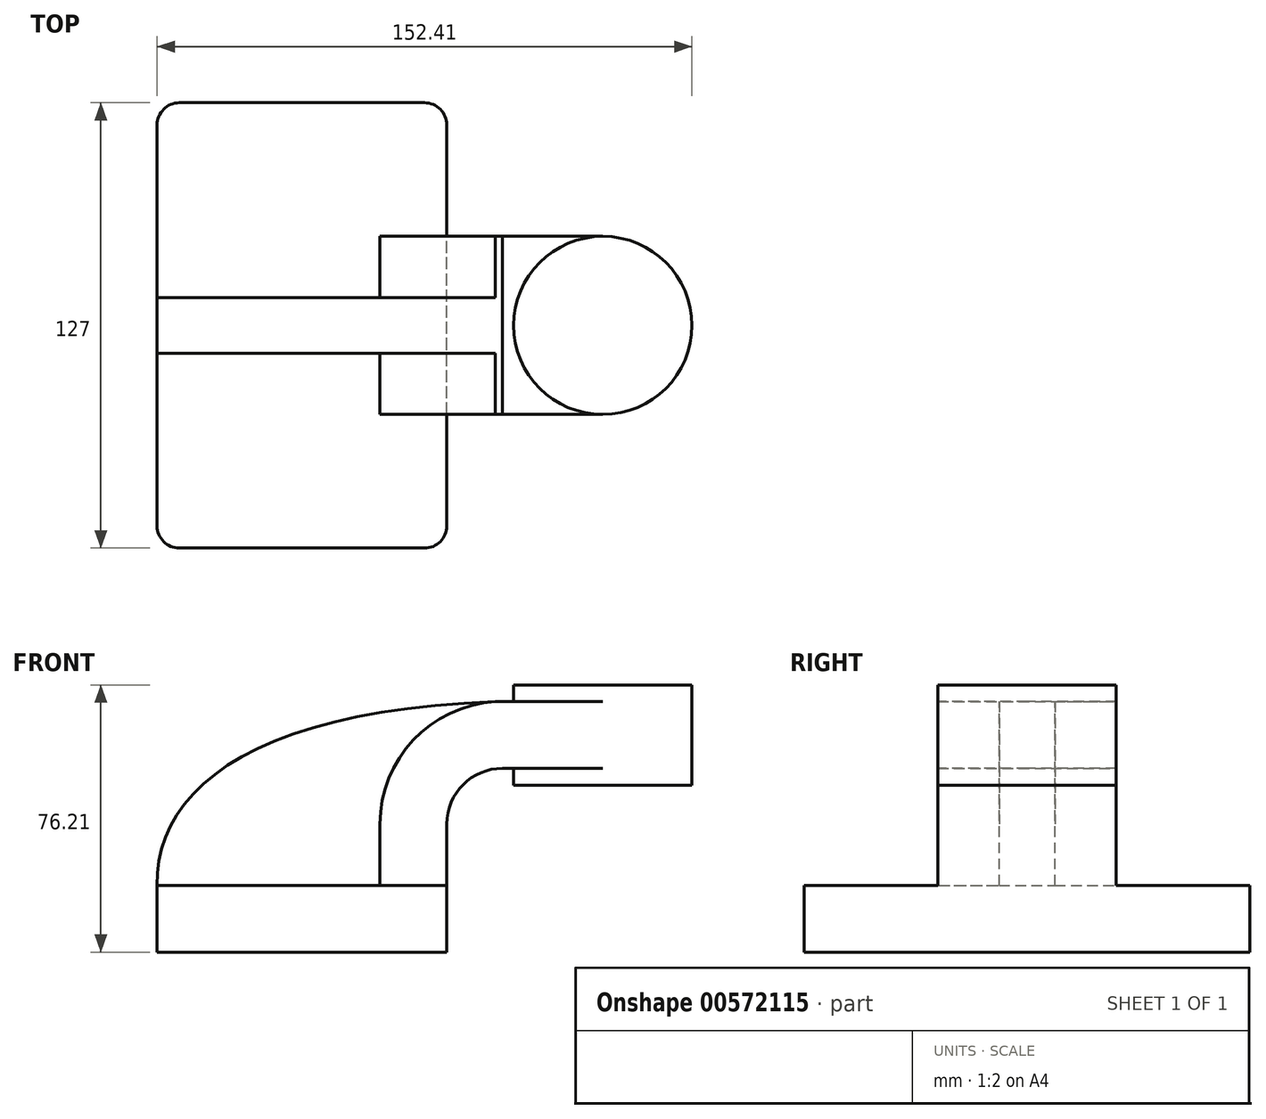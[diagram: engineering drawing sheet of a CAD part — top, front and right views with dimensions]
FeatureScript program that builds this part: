
annotation { "Feature Type Name" : "Feature", "Feature Type Description" : "" }
export const myFeature = defineFeature(function(context is Context, id is Id, definition is map)
    precondition{}
    {
        {
            var Q0;
            Q0=qCreatedBy(makeId("Front.planeOp"),FACE);
            var sketch = newSketch(context, id + "F0", { "sketchPlane" : qUnion([Q0])});
            skLineSegment(sketch, "E0.bottom", {"start": v(41.28, -9.52) * mm, "end": v(-41.28, -9.53) * mm});
            skLineSegment(sketch, "E0.top", {"start": v(41.28, 9.53) * mm, "end": v(-41.28, 9.52) * mm});
            skLineSegment(sketch, "E0.left", {"start": v(41.28, -9.52) * mm, "end": v(41.28, 9.53) * mm});
            skLineSegment(sketch, "E0.right", {"start": v(-41.28, -9.53) * mm, "end": v(-41.28, 9.52) * mm});
            skPoint(sketch, "E0.middle", {"position": v(0, 0) * mm});
            skLineSegment(sketch, "E1.bottom", {"start": v(60.33, 38.1) * mm, "end": v(111.13, 38.1) * mm});
            skLineSegment(sketch, "E1.top", {"start": v(60.33, 66.68) * mm, "end": v(111.13, 66.68) * mm});
            skLineSegment(sketch, "E1.left", {"start": v(60.33, 38.1) * mm, "end": v(60.33, 66.68) * mm});
            skLineSegment(sketch, "E1.right", {"start": v(111.13, 38.1) * mm, "end": v(111.13, 66.68) * mm});
            skPoint(sketch, "E1.middle", {"position": v(85.73, 52.39) * mm});
            skLineSegment(sketch, "E2", {"start": v(41.28, 9.53) * mm, "end": v(41.28, 27) * mm});
            skArc(sketch, "E3", {"start": v(41.28, 27) * mm, "mid": v(45.92, 38.23) * mm, "end": v(57.15, 42.88) * mm});
            skLineSegment(sketch, "E4", {"start": v(57.15, 42.88) * mm, "end": v(85.73, 42.88) * mm});
            skLineSegment(sketch, "E5.0", {"start": v(57.15, 61.93) * mm, "end": v(85.73, 61.93) * mm});
            skArc(sketch, "E5.1", {"start": v(22.23, 27) * mm, "mid": v(32.45, 51.7) * mm, "end": v(57.15, 61.93) * mm});
            skLineSegment(sketch, "E5.2", {"start": v(22.23, 9.53) * mm, "end": v(22.23, 27) * mm});
            skLineSegment(sketch, "E6", {"start": v(85.73, 42.88) * mm, "end": v(85.73, 66.68) * mm});
            skFitSpline(sketch, "E7", {"points": [v(-41.28, 9.52) * mm, v(57.15, 61.93) * mm], "startDerivative": vector(-1.78, 81.87) * mm, "endDerivative": vector(211.67, 5.76) * mm});
            skLineSegment(sketch, "E8", {"start": v(85.73, 42.88) * mm, "end": v(85.72, 38.1) * mm});
            skSolve(sketch);
        }
        {
            var Q0;
            Q0=makeQuery(id+"F0.imprint","IMPRINT",FACE,{"disambiguationData":[TD([[makeQuery(id+"F0.imprint","IMPRINT",EDGE,{"derivedFrom":sQuery(id+"F0.wireOp",EDGE,"E0.bottom")}),-1.0]])]});
            extrude(context, id + "F1", {"entities" : qUnion([Q0]), "endBound" : BoundingType.SYMMETRIC, "depth" : 127 * mm, "offsetDistance" : 25.4 * mm});
        }
        {
            var Q0;
            {var subQ6=sQuery(id+"F0.wireOp",EDGE,"E2");Q0=makeQuery(id+"F0.imprint","IMPRINT",FACE,{"disambiguationData":[TD([[makeQuery(id+"F0.imprint","IMPRINT",EDGE,{"derivedFrom":subQ6}),1.0]])]});}
            var Q1;
            {var subQ0=sQuery(id+"F0.wireOp",EDGE,"E4");var subQ1=sQuery(id+"F0.wireOp",EDGE,"E1.left");var subQ2=makeQuery(id+"F0.imprint","INTERSECT",VERTEX,{"derivedFrom":[subQ1,subQ0]});Q1=makeQuery(id+"F0.imprint","IMPRINT",FACE,{"disambiguationData":[TD([[makeQuery(id+"F0.imprint","IMPRINT",EDGE,{"disambiguationData":[TD([[subQ2,-1.0]])],"derivedFrom":subQ1}),-1.0]])]});}
            extrude(context, id + "F2", {"entities" : qUnion([Q0, Q1]), "operationType" : NewBodyOperationType.ADD, "endBound" : BoundingType.SYMMETRIC, "depth" : 50.8 * mm, "offsetDistance" : 25.4 * mm});
        }
        {
            var Q0;
            {var subQ3=sQuery(id+"F0.wireOp",EDGE,"E5.2");Q0=makeQuery(id+"F0.imprint","IMPRINT",FACE,{"disambiguationData":[TD([[makeQuery(id+"F0.imprint","IMPRINT",EDGE,{"derivedFrom":subQ3}),1.0]])]});}
            extrude(context, id + "F3", {"entities" : qUnion([Q0]), "operationType" : NewBodyOperationType.ADD, "endBound" : BoundingType.SYMMETRIC, "depth" : 15.88 * mm, "offsetDistance" : 25.4 * mm});
        }
        {
            var Q0;
            {var subQ3=sQuery(id+"F0.wireOp",EDGE,"E1.right");Q0=makeQuery(id+"F0.imprint","IMPRINT",FACE,{"disambiguationData":[TD([[makeQuery(id+"F0.imprint","IMPRINT",EDGE,{"derivedFrom":subQ3}),1.0]])]});}
            var Q1;
            Q1=sQuery(id+"F0.wireOp",EDGE,"E6");
            revolve(context, id + "F4", {"operationType" : NewBodyOperationType.ADD, "entities" : qUnion([Q0]), "axis" : qUnion([Q1]), "revolveType" : RevolveType.FULL});
        }
        {
            var Q0;
            Q0=makeQuery(id+"F1.opExtrude","CAP_EDGE",EDGE,{"disambiguationData":[OSD([sQuery(id+"F0.wireOp",EDGE,"E0.right")])],"isStart":false});
            var Q1;
            Q1=makeQuery(id+"F1.opExtrude","CAP_EDGE",EDGE,{"disambiguationData":[OSD([sQuery(id+"F0.wireOp",EDGE,"E0.left")])],"isStart":false});
            var Q2;
            Q2=makeQuery(id+"F1.opExtrude","CAP_EDGE",EDGE,{"disambiguationData":[OSD([sQuery(id+"F0.wireOp",EDGE,"E0.right")])],"isStart":true});
            var Q3;
            Q3=makeQuery(id+"F1.opExtrude","CAP_EDGE",EDGE,{"disambiguationData":[OSD([sQuery(id+"F0.wireOp",EDGE,"E0.left")])],"isStart":true});
            fillet(context, id + "F5", {"entities" : qUnion([Q0, Q1, Q2, Q3]), "radius" : 6.35 * mm, "tangentPropagation" : true, "allowEdgeOverflow" : false});
        }
    });
